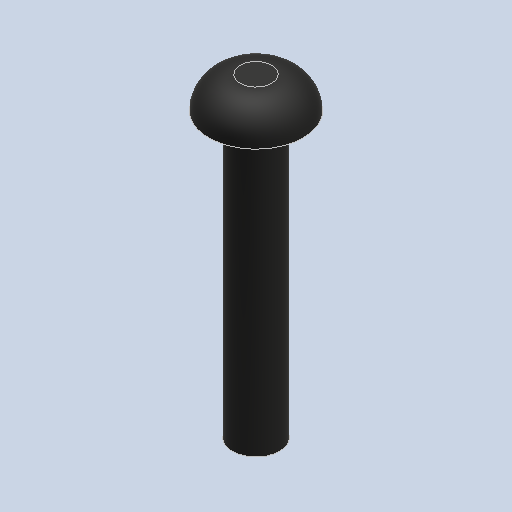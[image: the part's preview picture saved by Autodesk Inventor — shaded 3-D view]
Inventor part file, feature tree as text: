
AUTODESK INVENTOR PART (.ipt)
format: ipt  version: 2023 (Build 270158030, 158C)  size: 245,760 bytes
history: native  units: mm
features: extrude x2, sketch x2, other x1, fillet x1
ambient origin geometry x8: Origin, YZ Plane, XZ Plane, XY Plane, X Axis, Y Axis, Z Axis, Center Point
bodies: Body1 (feature_tree)
feature tree (6):
  other  "ソリッド1"
  extrude  "押し出し1"  Depth=3.0mm
  extrude  "押し出し2"  Depth=18.0mm TaperAngle=0.0deg
  fillet  "フィレット1"  Radius=6.0mm
  sketch  "スケッチ1"
  sketch  "スケッチ2"
